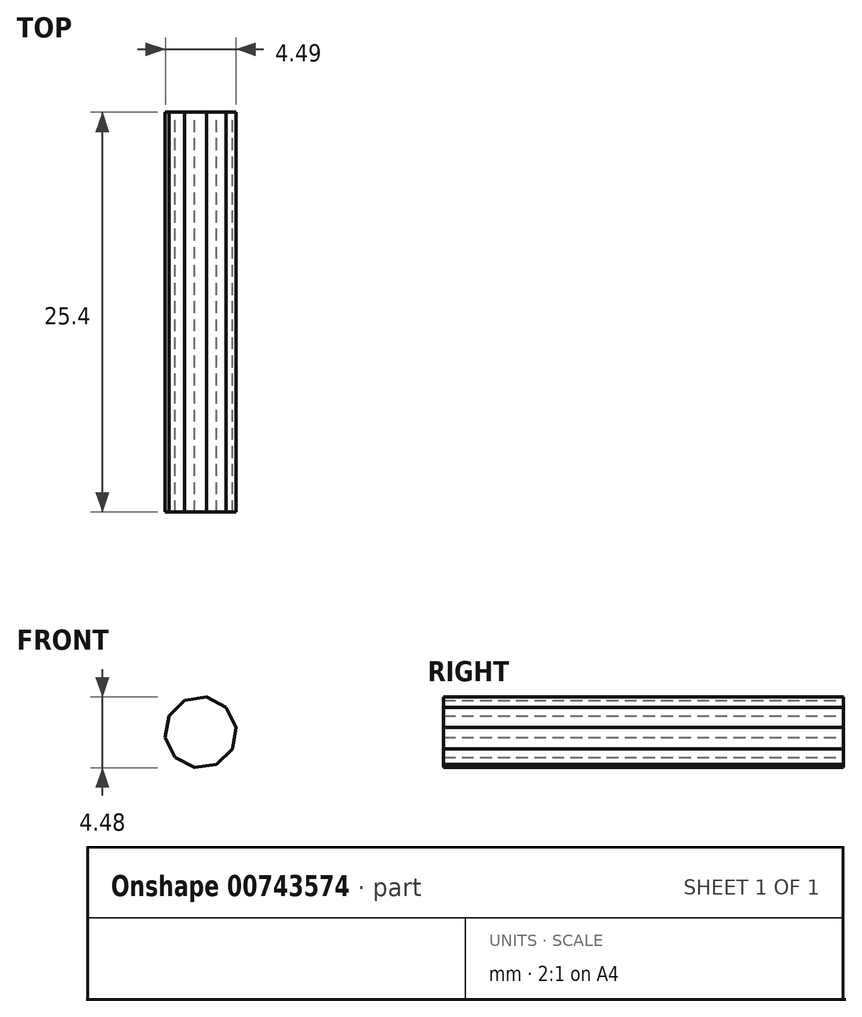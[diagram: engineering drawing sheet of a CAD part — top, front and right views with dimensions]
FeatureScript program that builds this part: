
annotation { "Feature Type Name" : "Feature", "Feature Type Description" : "" }
export const myFeature = defineFeature(function(context is Context, id is Id, definition is map)
    precondition{}
    {
        {
            var Q0;
            Q0=qCreatedBy(makeId("Front.planeOp"),FACE);
            var sketch = newSketch(context, id + "F0", { "sketchPlane" : qUnion([Q0])});
            skCircle(sketch, "E0.cCircle", {"center": v(-40.26, 35.05) * mm, "radius": 2.27 * mm, "construction": true});
            skLineSegment(sketch, "E0.0", {"start": v(-39.88, 37.29) * mm, "end": v(-38.64, 36.64) * mm});
            skLineSegment(sketch, "E0.1", {"start": v(-38.64, 36.64) * mm, "end": v(-38.01, 35.38) * mm});
            skLineSegment(sketch, "E0.2", {"start": v(-38.01, 35.38) * mm, "end": v(-38.25, 34) * mm});
            skLineSegment(sketch, "E0.3", {"start": v(-38.25, 34) * mm, "end": v(-39.25, 33.02) * mm});
            skLineSegment(sketch, "E0.4", {"start": v(-39.25, 33.02) * mm, "end": v(-40.64, 32.81) * mm});
            skLineSegment(sketch, "E0.5", {"start": v(-40.64, 32.81) * mm, "end": v(-41.88, 33.46) * mm});
            skLineSegment(sketch, "E0.6", {"start": v(-41.88, 33.46) * mm, "end": v(-42.5, 34.72) * mm});
            skLineSegment(sketch, "E0.7", {"start": v(-42.5, 34.72) * mm, "end": v(-42.27, 36.1) * mm});
            skLineSegment(sketch, "E0.8", {"start": v(-42.27, 36.1) * mm, "end": v(-41.27, 37.09) * mm});
            skLineSegment(sketch, "E0.9", {"start": v(-41.27, 37.09) * mm, "end": v(-39.88, 37.29) * mm});
            skSolve(sketch);
        }
        {
            var Q0;
            Q0 = qSketchRegion(id + "F0", true);
            extrude(context, id + "F1", {"entities" : qUnion([Q0]), "depth" : 25.4 * mm, "offsetDistance" : 25.4 * mm});
        }
    });
